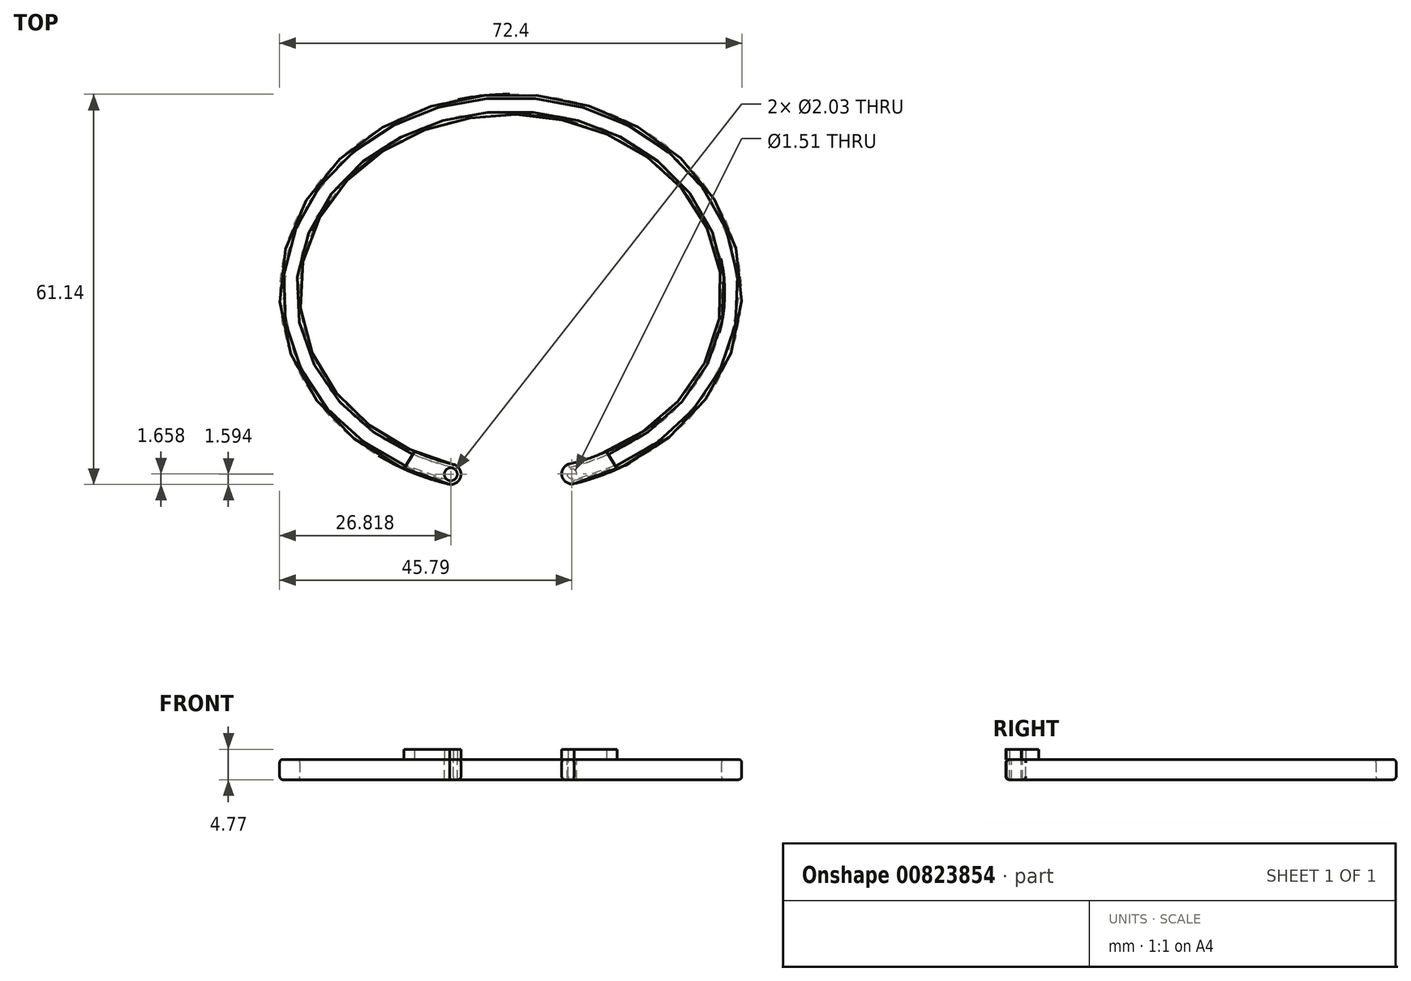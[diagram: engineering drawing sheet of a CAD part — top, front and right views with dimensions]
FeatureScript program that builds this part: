
annotation { "Feature Type Name" : "Feature", "Feature Type Description" : "" }
export const myFeature = defineFeature(function(context is Context, id is Id, definition is map)
    precondition{}
    {
        {
            var Q0;
            Q0=qCreatedBy(makeId("Top.planeOp"),FACE);
            var sketch = newSketch(context, id + "F0", { "sketchPlane" : qUnion([Q0])});
            skPoint(sketch, "E0", {"position": v(-9.38, -28.44) * mm});
            skCircle(sketch, "E1", {"center": v(-9.38, -28.44) * mm, "radius": 1.02 * mm});
            skEllipse(sketch, "E2", {"center": v(0, 0) * mm, "majorRadius": 34.6 * mm, "minorRadius": 29.53 * mm, "majorAxis": v(1, 0)});
            skPoint(sketch, "E3", {"position": v(-15.87, -26.24) * mm});
            skPoint(sketch, "E4", {"position": v(15.88, -27.95) * mm});
            skPoint(sketch, "E5", {"position": v(15.88, -26.24) * mm});
            skLineSegment(sketch, "E6", {"start": v(-15.87, -26.24) * mm, "end": v(0, 0) * mm});
            skLineSegment(sketch, "E7", {"start": v(0, 0) * mm, "end": v(15.88, -26.24) * mm});
            skEllipse(sketch, "E8", {"center": v(0, 0) * mm, "majorRadius": 36.2 * mm, "minorRadius": 31.12 * mm, "majorAxis": v(1, 0)});
            skLineSegment(sketch, "E9", {"start": v(15.88, -26.24) * mm, "end": v(16.7, -27.61) * mm});
            skLineSegment(sketch, "E10", {"start": v(-15.87, -26.24) * mm, "end": v(-16.7, -27.61) * mm});
            skEllipse(sketch, "E11", {"center": v(0, 0) * mm, "majorRadius": 33.02 * mm, "minorRadius": 27.94 * mm, "majorAxis": v(1, 0)});
            skPoint(sketch, "E12.0", {"position": v(9.6, -28.37) * mm});
            skArc(sketch, "E13", {"start": v(-9.97, -29.92) * mm, "mid": v(-7.87, -28.94) * mm, "end": v(-8.96, -26.9) * mm});
            skArc(sketch, "E14", {"start": v(9.02, -26.88) * mm, "mid": v(8.08, -28.88) * mm, "end": v(10.03, -29.9) * mm});
            skSolve(sketch);
        }
        {
            var Q0;
            {var subQ0=sQuery(id+"F0.wireOp",EDGE,"E9");Q0=makeQuery(id+"F0.imprint","IMPRINT",FACE,{"disambiguationData":[TD([[makeQuery(id+"F0.imprint","IMPRINT",EDGE,{"derivedFrom":subQ0}),-1.0]])]});}
            var Q1;
            {var subQ2=sQuery(id+"F0.wireOp",EDGE,"E9");Q1=makeQuery(id+"F0.imprint","IMPRINT",FACE,{"disambiguationData":[TD([[makeQuery(id+"F0.imprint","IMPRINT",EDGE,{"derivedFrom":subQ2}),1.0]])]});}
            var Q2;
            {var subQ0=sQuery(id+"F0.wireOp",EDGE,"E6");var subQ5=sQuery(id+"F0.wireOp",EDGE,"E11");var subQ6=makeQuery(id+"F0.imprint","INTERSECT",VERTEX,{"derivedFrom":[subQ0,subQ5]});Q2=makeQuery(id+"F0.imprint","IMPRINT",FACE,{"disambiguationData":[TD([[makeQuery(id+"F0.imprint","IMPRINT",EDGE,{"disambiguationData":[TD([[subQ6,1.0]])],"derivedFrom":subQ5}),-1.0]])]});}
            var Q3;
            {var subQ3=sQuery(id+"F0.wireOp",EDGE,"E14");var subQ5=sQuery(id+"F0.wireOp",EDGE,"E11");var subQ7=makeQuery(id+"F0.imprint","INTERSECT",VERTEX,{"derivedFrom":[subQ5,subQ3]});Q3=makeQuery(id+"F0.imprint","IMPRINT",FACE,{"disambiguationData":[TD([[makeQuery(id+"F0.imprint","IMPRINT",EDGE,{"disambiguationData":[TD([[subQ7,-1.0]])],"derivedFrom":subQ5}),-1.0]])]});}
            var Q4;
            {var subQ5=sQuery(id+"F0.wireOp",EDGE,"E10");Q4=makeQuery(id+"F0.imprint","IMPRINT",FACE,{"disambiguationData":[TD([[makeQuery(id+"F0.imprint","IMPRINT",EDGE,{"derivedFrom":subQ5}),1.0]])]});}
            var Q5;
            {var subQ1=sQuery(id+"F0.wireOp",EDGE,"E2");var subQ5=sQuery(id+"F0.wireOp",EDGE,"E1");var subQ9=makeQuery(id+"F0.imprint","INTERSECT",VERTEX,{"disambiguationData":[OD(0.0)],"derivedFrom":[subQ5,subQ1]});Q5=makeQuery(id+"F0.imprint","IMPRINT",FACE,{"disambiguationData":[TD([[makeQuery(id+"F0.imprint","IMPRINT",EDGE,{"disambiguationData":[TD([[subQ9,1.0]])],"derivedFrom":subQ5}),-1.0]])]});}
            extrude(context, id + "F1", {"entities" : qUnion([Q0, Q1, Q2, Q3, Q4, Q5]), "oppositeDirection" : true, "depth" : 3.17 * mm, "offsetDistance" : 25.4 * mm});
        }
        {
            var Q0;
            Q0=makeQuery(id+"F1.opExtrude","CAP_FACE",FACE,{"disambiguationData":[OSD([sQuery(id+"F0.wireOp",EDGE,"E1"),sQuery(id+"F0.wireOp",EDGE,"E8"),sQuery(id+"F0.wireOp",EDGE,"E11"),sQuery(id+"F0.wireOp",EDGE,"E13"),sQuery(id+"F0.wireOp",EDGE,"E14")])],"isStart":true});
            var sketch = newSketch(context, id + "F2", { "sketchPlane" : qUnion([Q0])});
            skPoint(sketch, "E15.0", {"position": v(9.6, -28.37) * mm});
            skSolve(sketch);
        }
        {
            var Q0;
            Q0=sQuery(id+"F2.wireOp",VERTEX,"E15.0");
            var Q1;
            Q1=makeQuery(id+"F5.opExtrude","SWEPT_BODY",BODY,{"disambiguationData":[OSD([sQuery(id+"F0.wireOp",EDGE,"E7"),sQuery(id+"F0.wireOp",EDGE,"E8"),sQuery(id+"F0.wireOp",EDGE,"E9"),sQuery(id+"F0.wireOp",EDGE,"E11"),sQuery(id+"F0.wireOp",EDGE,"E14")])]});
            var Q2;
            Q2=makeQuery(id+"F1.opExtrude","SWEPT_BODY",BODY,{"disambiguationData":[OSD([sQuery(id+"F0.wireOp",EDGE,"E1"),sQuery(id+"F0.wireOp",EDGE,"E8"),sQuery(id+"F0.wireOp",EDGE,"E11"),sQuery(id+"F0.wireOp",EDGE,"E13"),sQuery(id+"F0.wireOp",EDGE,"E14")])]});
            hole(context, id + "F3", {"style" : HoleStyle.SIMPLE, "endStyle" : HoleEndStyle.BLIND, "standardTappedOrClearance" : lookupTablePath({ "standard" : "ANSI", "engagement" : "75%", "pitch" : "64 tpi", "size" : "#1", "type" : "Tapped" }), "standardBlindInLast" : lookupTablePath({ "standard" : "ANSI", "engagement" : "75%", "pitch" : "64 tpi", "size" : "#1", "type" : "Tapped" }), "holeDiameter" : 1.51 * mm, "majorDiameter" : 1.85 * mm, "showTappedDepth" : true, "holeDepth" : 13.9 * mm, "isTappedThrough" : true, "tappedDepth" : 12.71 * mm, "tapClearance" : 3, "locations" : qUnion([Q0]), "scope" : qUnion([Q1, Q2])});
        }
        {
            var Q0;
            Q0=makeQuery(id+"F1.opExtrude","CAP_EDGE",EDGE,{"disambiguationData":[OSD([sQuery(id+"F0.wireOp",EDGE,"E8")])],"isStart":true});
            var Q1;
            Q1=makeQuery(id+"F1.opExtrude","CAP_EDGE",EDGE,{"disambiguationData":[OSD([sQuery(id+"F0.wireOp",EDGE,"E11")])],"isStart":true});
            var Q2;
            Q2=makeQuery(id+"F1.opExtrude","CAP_EDGE",EDGE,{"disambiguationData":[OSD([sQuery(id+"F0.wireOp",EDGE,"E8")])],"isStart":false});
            var Q3;
            Q3=makeQuery(id+"F1.opExtrude","CAP_EDGE",EDGE,{"disambiguationData":[OSD([sQuery(id+"F0.wireOp",EDGE,"E11")])],"isStart":false});
            var Q4;
            Q4=makeQuery(id+"F1.opExtrude","CAP_EDGE",EDGE,{"disambiguationData":[OSD([sQuery(id+"F0.wireOp",EDGE,"E13")])],"isStart":false});
            var Q5;
            Q5=makeQuery(id+"F1.opExtrude","CAP_EDGE",EDGE,{"disambiguationData":[OSD([sQuery(id+"F0.wireOp",EDGE,"E14")])],"isStart":false});
            var Q6;
            Q6=makeQuery(id+"F5.opExtrude","SWEPT_EDGE",EDGE,{"disambiguationData":[OSD([sQuery(id+"F0.wireOp",EDGE,"E8"),sQuery(id+"F0.wireOp",EDGE,"E10")])]});
            var Q7;
            Q7=makeQuery(id+"F5.opExtrude","SWEPT_EDGE",EDGE,{"disambiguationData":[OSD([sQuery(id+"F0.wireOp",EDGE,"E6"),sQuery(id+"F0.wireOp",EDGE,"E11")])]});
            var Q8;
            Q8=makeQuery(id+"F5.opExtrude","SWEPT_EDGE",EDGE,{"disambiguationData":[OSD([sQuery(id+"F0.wireOp",EDGE,"E8"),sQuery(id+"F0.wireOp",EDGE,"E9")])]});
            var Q9;
            Q9=makeQuery(id+"F5.opExtrude","SWEPT_EDGE",EDGE,{"disambiguationData":[OSD([sQuery(id+"F0.wireOp",EDGE,"E7"),sQuery(id+"F0.wireOp",EDGE,"E11")])]});
            var Q10;
            Q10=makeQuery(id+"F1.opExtrude","CAP_EDGE",EDGE,{"disambiguationData":[OSD([sQuery(id+"F0.wireOp",EDGE,"E14")])],"isStart":true});
            var Q11;
            Q11=makeQuery(id+"F1.opExtrude","CAP_EDGE",EDGE,{"disambiguationData":[OSD([sQuery(id+"F0.wireOp",EDGE,"E13")])],"isStart":true});
            fillet(context, id + "F4", {"entities" : qUnion([Q0, Q1, Q2, Q3, Q4, Q5, Q6, Q7, Q8, Q9, Q10, Q11]), "radius" : 0.5 * mm, "tangentPropagation" : true, "allowEdgeOverflow" : false});
        }
        {
            var Q0;
            {var subQ3=sQuery(id+"F0.wireOp",EDGE,"E14");var subQ5=sQuery(id+"F0.wireOp",EDGE,"E11");var subQ7=makeQuery(id+"F0.imprint","INTERSECT",VERTEX,{"derivedFrom":[subQ5,subQ3]});Q0=makeQuery(id+"F0.imprint","IMPRINT",FACE,{"disambiguationData":[TD([[makeQuery(id+"F0.imprint","IMPRINT",EDGE,{"disambiguationData":[TD([[subQ7,-1.0]])],"derivedFrom":subQ5}),-1.0]])]});}
            var Q1;
            {var subQ0=sQuery(id+"F0.wireOp",EDGE,"E9");Q1=makeQuery(id+"F0.imprint","IMPRINT",FACE,{"disambiguationData":[TD([[makeQuery(id+"F0.imprint","IMPRINT",EDGE,{"derivedFrom":subQ0}),-1.0]])]});}
            var Q2;
            {var subQ1=sQuery(id+"F0.wireOp",EDGE,"E2");var subQ5=sQuery(id+"F0.wireOp",EDGE,"E1");var subQ9=makeQuery(id+"F0.imprint","INTERSECT",VERTEX,{"disambiguationData":[OD(0.0)],"derivedFrom":[subQ5,subQ1]});Q2=makeQuery(id+"F0.imprint","IMPRINT",FACE,{"disambiguationData":[TD([[makeQuery(id+"F0.imprint","IMPRINT",EDGE,{"disambiguationData":[TD([[subQ9,1.0]])],"derivedFrom":subQ5}),-1.0]])]});}
            var Q3;
            {var subQ5=sQuery(id+"F0.wireOp",EDGE,"E10");Q3=makeQuery(id+"F0.imprint","IMPRINT",FACE,{"disambiguationData":[TD([[makeQuery(id+"F0.imprint","IMPRINT",EDGE,{"derivedFrom":subQ5}),1.0]])]});}
            extrude(context, id + "F5", {"entities" : qUnion([Q0, Q1, Q2, Q3]), "depth" : 1.59 * mm, "offsetDistance" : 25.4 * mm});
        }
    });
